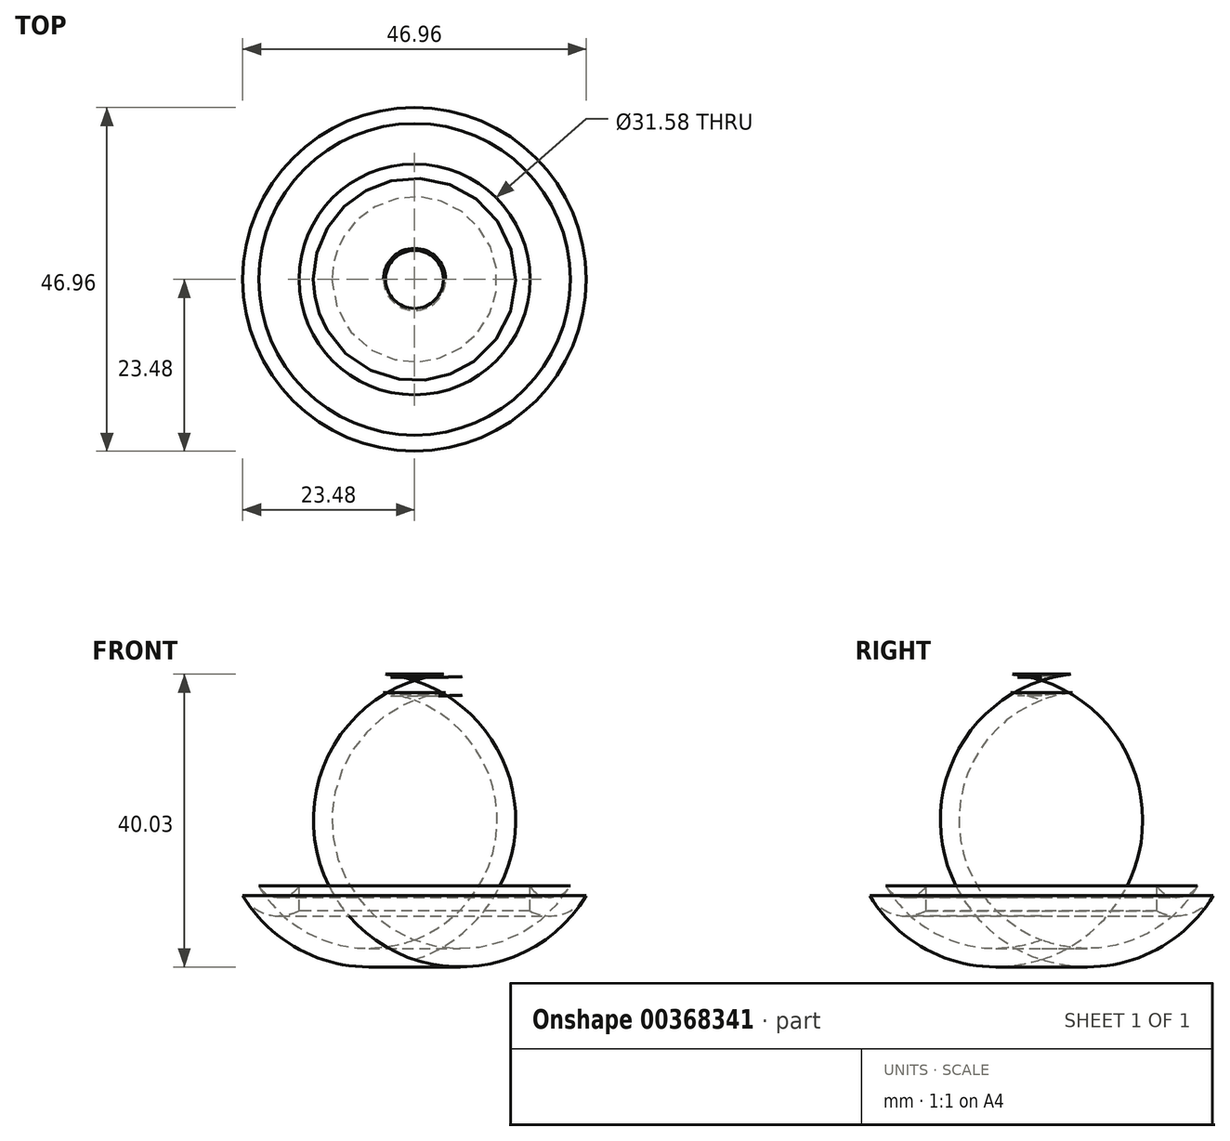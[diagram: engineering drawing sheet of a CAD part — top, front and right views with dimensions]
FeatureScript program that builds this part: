
annotation { "Feature Type Name" : "Feature", "Feature Type Description" : "" }
export const myFeature = defineFeature(function(context is Context, id is Id, definition is map)
    precondition{}
    {
        {
            var Q0;
            Q0=qCreatedBy(makeId("Front.planeOp"),FACE);
            var sketch = newSketch(context, id + "F0", { "sketchPlane" : qUnion([Q0])});
            skArc(sketch, "E0", {"start": v(-4.25, 21.32) * mm, "mid": v(-21, 13.4) * mm, "end": v(-21.3, -5.12) * mm});
            skLineSegment(sketch, "E1", {"start": v(-18.54, -9.23) * mm, "end": v(0, -9.23) * mm, "construction": true});
            skArc(sketch, "E2", {"start": v(-21.3, -5.12) * mm, "mid": v(-18.54, -6.69) * mm, "end": v(-15.79, -5.12) * mm});
            skArc(sketch, "E3.0", {"start": v(-23.48, -6.43) * mm, "mid": v(-20.06, -9.02) * mm, "end": v(-15.79, -8.52) * mm});
            skArc(sketch, "E3.1", {"start": v(-3.96, 23.84) * mm, "mid": v(-23.13, 14.77) * mm, "end": v(-23.48, -6.43) * mm});
            skArc(sketch, "E4", {"start": v(-3.96, 23.84) * mm, "mid": v(-1.98, 23.64) * mm, "end": v(0, 23.51) * mm});
            skLineSegment(sketch, "E5", {"start": v(-3.68, 23.43) * mm, "end": v(0, 23.43) * mm, "construction": true});
            skArc(sketch, "E6.0", {"start": v(-4.25, 21.32) * mm, "mid": v(-2.13, 21.1) * mm, "end": v(0, 20.97) * mm});
            skLineSegment(sketch, "E7", {"start": v(0, 23.51) * mm, "end": v(0, 20.97) * mm});
            skLineSegment(sketch, "E8", {"start": v(-15.79, -5.12) * mm, "end": v(-15.79, -8.52) * mm});
            skSolve(sketch);
        }
        {
            var Q0;
            Q0 = qSketchRegion(id + "F0", true);
            var Q1;
            Q1=sQuery(id+"F0.wireOp",EDGE,"E7");
            revolve(context, id + "F1", {"entities" : qUnion([Q0]), "axis" : qUnion([Q1]), "revolveType" : RevolveType.FULL});
        }
    });
